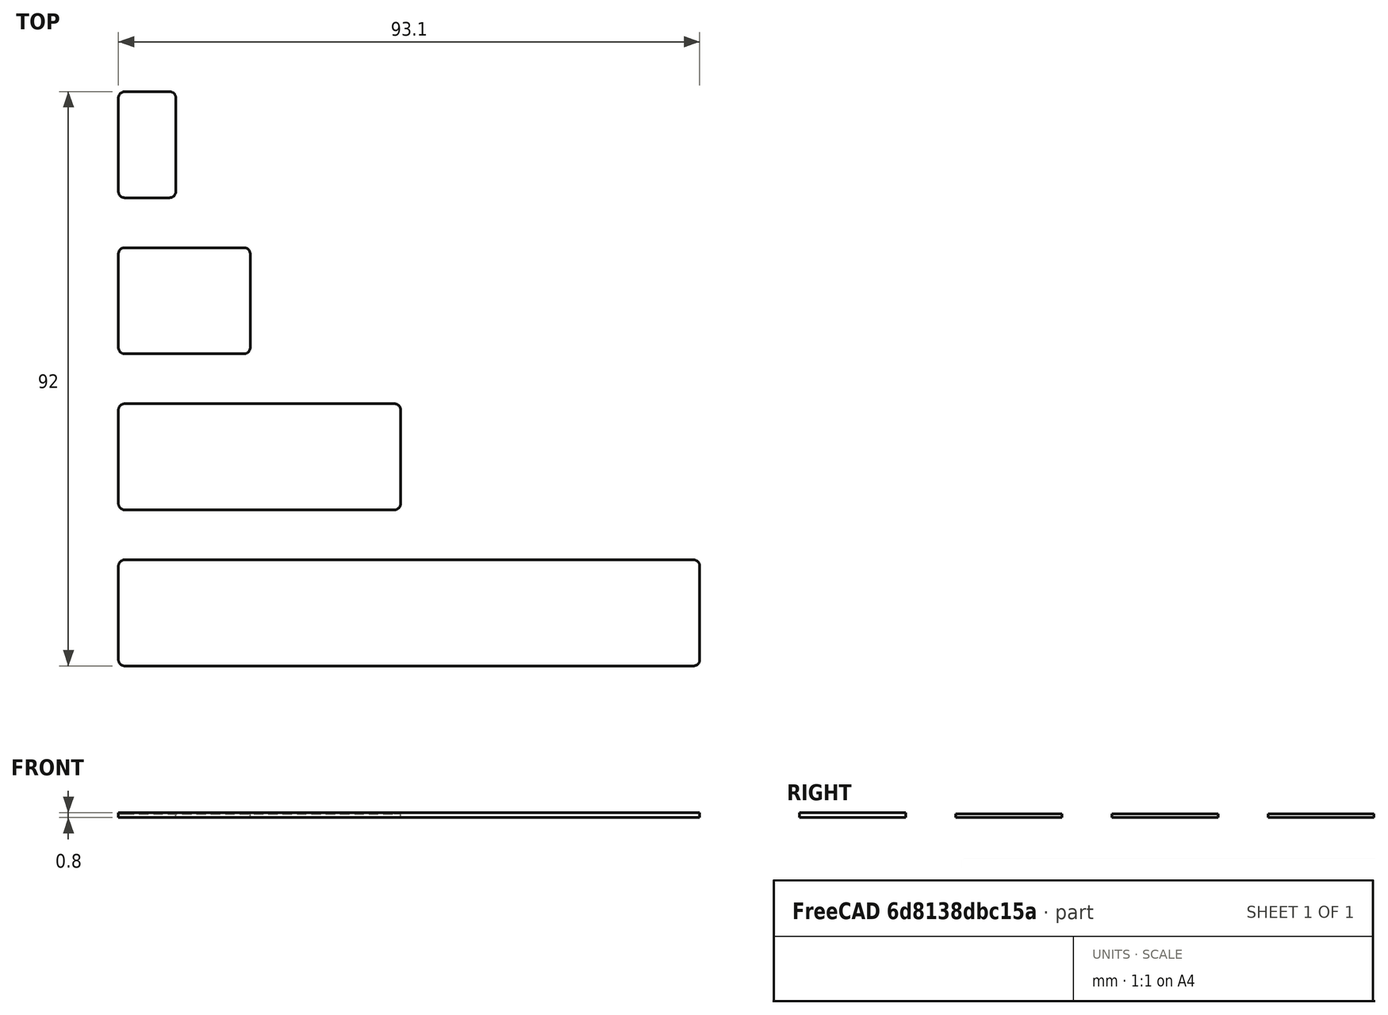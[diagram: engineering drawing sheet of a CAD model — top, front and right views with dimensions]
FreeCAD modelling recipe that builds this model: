
FCSTD DOCUMENT  (FreeCAD 0.16R)
Label: separators
License: All rights reserved
LicenseURL: http://en.wikipedia.org/wiki/All_rights_reserved
objects: Part::Box×4, Part::Fillet×4
note: 8 computed .brp shape members not serialized (recipe doc carries the construction recipe); baked Part::Feature solids carry a one-line shape summary decoded from their .brp

FEATURE [Part::Box] Box  label="Cube"
  Height = 0.8
  Length = 93.1
  Width = 17
FEATURE [Part::Fillet] Fillet  label="BigSeparator"
  Base = -> Box
  Edges = 4 edges r=1: [Edge1,Edge3,Edge5,Edge7]
FEATURE [Part::Box] Box001  label="Cube001"
  Height = 0.6
  Length = 45.2
  Width = 17
FEATURE [Part::Fillet] Fillet001  label="StandardSeparator"
  Base = -> Box001
  Edges = 4 edges r=1: [Edge1,Edge3,Edge5,Edge7]
  Placement = pos=(0,25,0) rot=(0,0,1;0rad)
FEATURE [Part::Box] Box002  label="Cube002"
  Height = 0.6
  Length = 21.1
  Width = 17
FEATURE [Part::Fillet] Fillet002  label="SmallSeparator"
  Base = -> Box002
  Edges = 4 edges r=1: [Edge1,Edge3,Edge5,Edge7]
  Placement = pos=(0,50,0) rot=(0,0,1;0rad)
FEATURE [Part::Box] Box003  label="Cube003"
  Height = 0.6
  Length = 9.2
  Width = 17
FEATURE [Part::Fillet] Fillet003  label="TinySeparator"
  Base = -> Box003
  Edges = 4 edges r=1: [Edge1,Edge3,Edge5,Edge7]
  Placement = pos=(0,75,0) rot=(0,0,1;0rad)
